# Revit family: Deca_Chuveiro Dream_1976.C.ST_Sem Tubo
name_source: partatom
category: Plumbing Fixtures
revit_build: Autodesk Revit Architecture 2012 (Build: 20120126_0600(x64)
units: mm (PartAtom-declared; Revit-internal decimal feet)

## types (2) — shared parameters
Aprovado por = Contino/quattroD
Assembly Code = D2020
Atendimento ao Cliente = 0800-0117075
Consumo = Varia com a pressão (consultar catálogo)
Criado por = Contino/quattroD
Description = Chuveiro
Diâmetro Ponto de Agua = 15 mm  [stored 0.0492126 ft]
Flow Pressure = 0.00 psi
Informações Complementares = Recomendável com pressão mínima de 6 m.c.a para aquecedor de passagem e de 4 m.c.a. para aquecedor de acumulação.
Linha = Dream
Louça/Metais = Metal
Manufacturer = Deca
Material = Deca_Latão Cromado e Plástico de Engenharia
Norma = ABNT NBR 15206:2005
Peso Liquido (Kg) = 1.86
Pressão = 2 A 40 mca
Produto = Chuveiro Dream sem tubo
Raio Ponto de Agua = 8 mm  [stored 0.0262467 ft]
Segmento = Luxo
URL = www.deca.com.br/produtos
Variações de COR = Cromado (1976.C.ST); Gold (1976.GL.ST)
zero-valued in all types: CWFU, Default Elevation, HWFU, WFU

## per-type parameters (varying)
| type | Chuveiro | Código | Model |
| 1976.C.ST_Cromado CR10 | Deca CR10 Cromado Metal | 1976.C.ST | 1976.C.ST |
| 1976.GL.ST_Gold GLD | Deca GLD Gold Metal | 1976.GL.ST | 1976.GL.ST |

note: [stored X ft] marks values corroborated as IEEE doubles in the binary element streams (Revit-internal decimal feet)

## geometry (parser evidence)
native form markers: Blend x4, Sweep x1
no freeform markers — native parametric forms only
